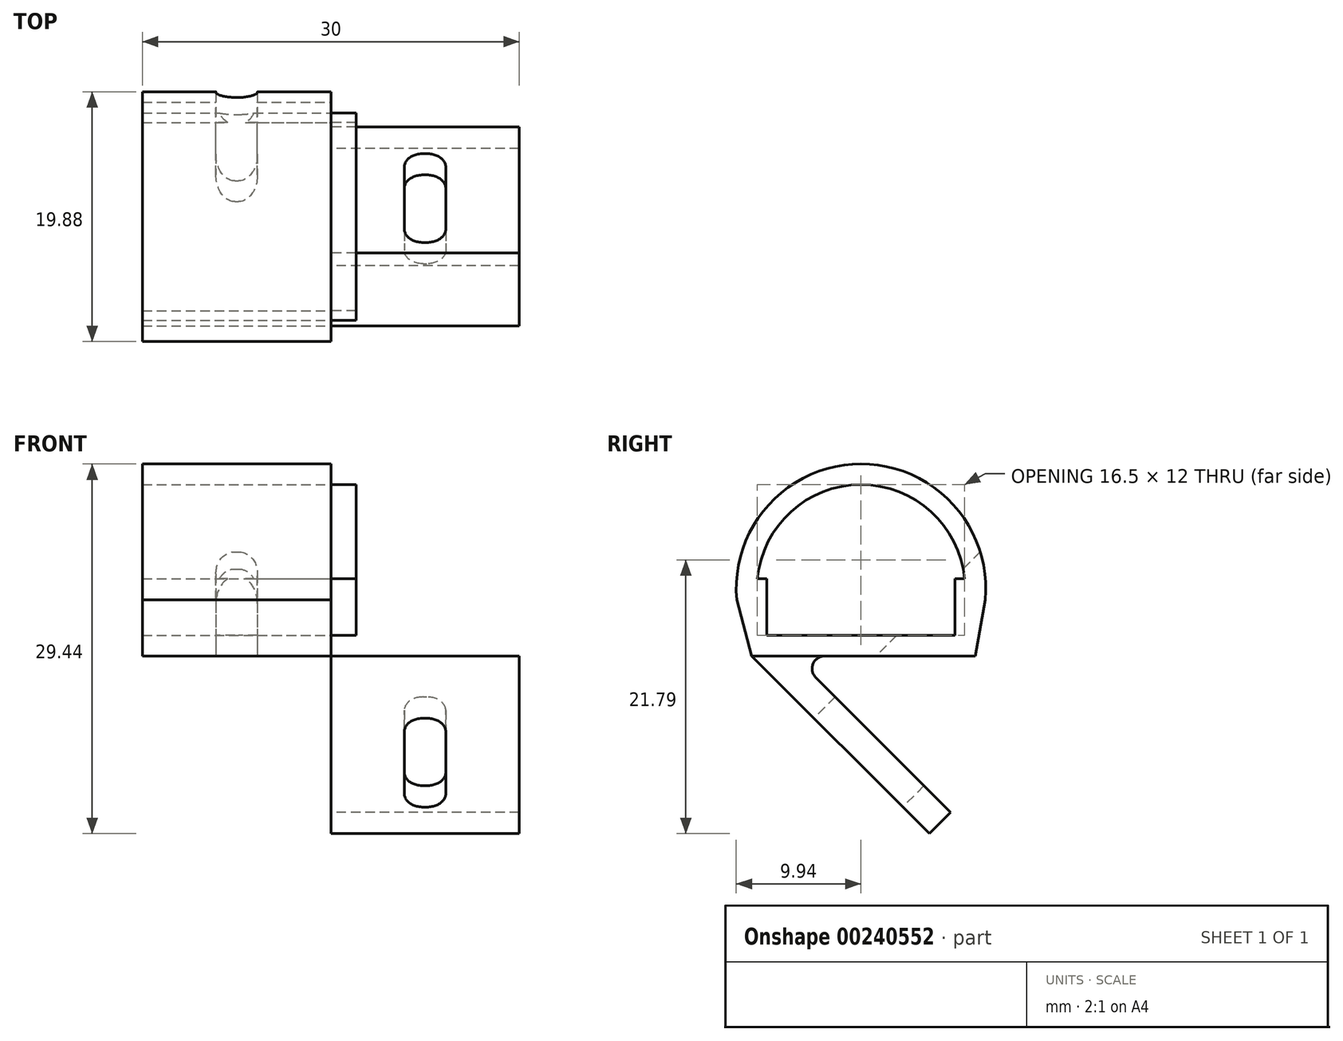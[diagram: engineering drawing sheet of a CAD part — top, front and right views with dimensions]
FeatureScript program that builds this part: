
annotation { "Feature Type Name" : "Feature", "Feature Type Description" : "" }
export const myFeature = defineFeature(function(context is Context, id is Id, definition is map)
    precondition{}
    {
        {
            var Q0;
            Q0=qCreatedBy(makeId("Right.planeOp"),FACE);
            var sketch = newSketch(context, id + "F0", { "sketchPlane" : qUnion([Q0])});
            skLineSegment(sketch, "E0.top", {"start": v(-7.5, -4.5) * mm, "end": v(7.5, -4.5) * mm});
            skLineSegment(sketch, "E0.left", {"start": v(-7.5, 0) * mm, "end": v(-7.5, -4.5) * mm});
            skLineSegment(sketch, "E0.right", {"start": v(7.5, 0) * mm, "end": v(7.5, -4.5) * mm});
            skLineSegment(sketch, "E1", {"start": v(-8.25, 0) * mm, "end": v(-7.5, 0) * mm});
            skArc(sketch, "E2", {"start": v(8.25, 0) * mm, "mid": v(0, 7.5) * mm, "end": v(-8.25, 0) * mm});
            skLineSegment(sketch, "E3", {"start": v(7.5, 0) * mm, "end": v(8.25, 0) * mm});
            skArc(sketch, "E4.3", {"start": v(9.9, -1.68) * mm, "mid": v(0, 9.15) * mm, "end": v(-9.9, -1.68) * mm});
            skLineSegment(sketch, "E4.4", {"start": v(-8.7, -6.15) * mm, "end": v(9.1, -6.15) * mm});
            skLineSegment(sketch, "E5", {"start": v(-9.9, -1.68) * mm, "end": v(-8.7, -6.15) * mm});
            skLineSegment(sketch, "E6", {"start": v(9.9, -1.68) * mm, "end": v(9.1, -6.15) * mm});
            skSolve(sketch);
        }
        {
            var Q0;
            Q0=makeQuery(id+"F0.imprint","IMPRINT",FACE,{"disambiguationData":[TD([[makeQuery(id+"F0.imprint","IMPRINT",EDGE,{"derivedFrom":sQuery(id+"F0.wireOp",EDGE,"E0.top")}),-1.0]])]});
            extrude(context, id + "F1", {"entities" : qUnion([Q0]), "depth" : 15 * mm});
        }
        {
            var Q0;
            Q0=makeQuery(id+"F0.imprint","IMPRINT",FACE,{"disambiguationData":[TD([[makeQuery(id+"F0.imprint","IMPRINT",EDGE,{"derivedFrom":sQuery(id+"F0.wireOp",EDGE,"E0.top")}),1.0]])]});
            extrude(context, id + "F2", {"entities" : qUnion([Q0]), "depth" : 2 * mm});
        }
        {
            var Q0;
            Q0=qCreatedBy(makeId("Right.planeOp"),FACE);
            var sketch = newSketch(context, id + "F3", { "sketchPlane" : qUnion([Q0])});
            skLineSegment(sketch, "E7.0", {"start": v(-2.9, -6.15) * mm, "end": v(9.1, -6.15) * mm});
            skLineSegment(sketch, "E8", {"start": v(-8.7, -6.15) * mm, "end": v(5.44, -20.3) * mm});
            skLineSegment(sketch, "E9", {"start": v(5.44, -20.3) * mm, "end": v(7.14, -18.6) * mm});
            skLineSegment(sketch, "E10", {"start": v(7.14, -18.6) * mm, "end": v(-3.6, -7.86) * mm});
            skPoint(sketch, "E11.newPointB", {"position": v(-8.7, -6.15) * mm});
            skArc(sketch, "E11.filletArc", {"start": v(-2.9, -6.15) * mm, "mid": v(-3.82, -6.77) * mm, "end": v(-3.6, -7.86) * mm});
            skLineSegment(sketch, "E12", {"start": v(-8.7, -6.15) * mm, "end": v(-2.9, -6.15) * mm});
            skSolve(sketch);
        }
        {
            var Q0;
            Q0=makeQuery(id+"F3.imprint","IMPRINT",FACE,{"disambiguationData":[TD([[makeQuery(id+"F3.imprint","IMPRINT",EDGE,{"derivedFrom":sQuery(id+"F3.wireOp",EDGE,"E8")}),1.0]])]});
            extrude(context, id + "F4", {"entities" : qUnion([Q0]), "depth" : 15 * mm});
        }
        {
            var Q0;
            Q0=makeQuery(id+"F4.opExtrude","SWEPT_FACE",FACE,{"disambiguationData":[OSD([sQuery(id+"F3.wireOp",EDGE,"E8")])]});
            var sketch = newSketch(context, id + "F5", { "sketchPlane" : qUnion([Q0])});
            skLineSegment(sketch, "E13.bottom", {"start": v(7.35, -15.2) * mm, "end": v(7.65, -15.2) * mm});
            skLineSegment(sketch, "E13.top", {"start": v(7.35, -5.2) * mm, "end": v(7.65, -5.2) * mm});
            skLineSegment(sketch, "E13.left", {"start": v(5.85, -13.7) * mm, "end": v(5.85, -6.7) * mm});
            skLineSegment(sketch, "E13.right", {"start": v(9.15, -13.7) * mm, "end": v(9.15, -6.7) * mm});
            skLineSegment(sketch, "E14.0.0", {"start": v(0, 1.8) * mm, "end": v(0, -18.2) * mm});
            skLineSegment(sketch, "E14.0.1", {"start": v(0, -18.2) * mm, "end": v(15, -18.2) * mm});
            skLineSegment(sketch, "E14.0.2", {"start": v(15, -18.2) * mm, "end": v(15, 1.8) * mm});
            skLineSegment(sketch, "E14.0.3", {"start": v(15, 1.8) * mm, "end": v(0, 1.8) * mm});
            skPoint(sketch, "E15.visualSharp", {"position": v(5.85, -15.2) * mm});
            skArc(sketch, "E15.filletArc", {"start": v(5.85, -13.7) * mm, "mid": v(6.29, -14.76) * mm, "end": v(7.35, -15.2) * mm});
            skPoint(sketch, "E16.visualSharp", {"position": v(9.15, -15.2) * mm});
            skArc(sketch, "E16.filletArc", {"start": v(7.65, -15.2) * mm, "mid": v(8.71, -14.76) * mm, "end": v(9.15, -13.7) * mm});
            skPoint(sketch, "E17.visualSharp", {"position": v(9.15, -5.2) * mm});
            skArc(sketch, "E17.filletArc", {"start": v(9.15, -6.7) * mm, "mid": v(8.71, -5.64) * mm, "end": v(7.65, -5.2) * mm});
            skPoint(sketch, "E18.visualSharp", {"position": v(5.85, -5.2) * mm});
            skArc(sketch, "E18.filletArc", {"start": v(7.35, -5.2) * mm, "mid": v(6.29, -5.64) * mm, "end": v(5.85, -6.7) * mm});
            skSolve(sketch);
        }
        {
            var Q0;
            Q0=makeQuery(id+"F5.imprint","IMPRINT",FACE,{"disambiguationData":[TD([[makeQuery(id+"F5.imprint","IMPRINT",EDGE,{"derivedFrom":sQuery(id+"F5.wireOp",EDGE,"E13.bottom")}),1.0]])]});
            extrude(context, id + "F6", {"entities" : qUnion([Q0]), "operationType" : NewBodyOperationType.REMOVE, "oppositeDirection" : true, "depth" : 25 * mm});
        }
        {
            var Q0;
            Q0=makeQuery(id+"F1.opExtrude","SWEPT_BODY",BODY,{"disambiguationData":[OSD([sQuery(id+"F0.wireOp",EDGE,"E0.top"),sQuery(id+"F0.wireOp",EDGE,"E0.left"),sQuery(id+"F0.wireOp",EDGE,"E0.right"),sQuery(id+"F0.wireOp",EDGE,"E1"),sQuery(id+"F0.wireOp",EDGE,"E2"),sQuery(id+"F0.wireOp",EDGE,"E3"),sQuery(id+"F0.wireOp",EDGE,"E4.3"),sQuery(id+"F0.wireOp",EDGE,"E4.4"),sQuery(id+"F0.wireOp",EDGE,"E5"),sQuery(id+"F0.wireOp",EDGE,"E6")])]});
            var Q1;
            Q1=qCreatedBy(makeId("Right.planeOp"),FACE);
            mirror(context, id + "F7", {"entities" : qUnion([Q0]), "mirrorPlane" : qUnion([Q1])});
        }
        {
            var Q0;
            Q0=makeQuery(id+"F1.opExtrude","SWEPT_BODY",BODY,{"disambiguationData":[OSD([sQuery(id+"F0.wireOp",EDGE,"E0.top"),sQuery(id+"F0.wireOp",EDGE,"E0.left"),sQuery(id+"F0.wireOp",EDGE,"E0.right"),sQuery(id+"F0.wireOp",EDGE,"E1"),sQuery(id+"F0.wireOp",EDGE,"E2"),sQuery(id+"F0.wireOp",EDGE,"E3"),sQuery(id+"F0.wireOp",EDGE,"E4.3"),sQuery(id+"F0.wireOp",EDGE,"E4.4"),sQuery(id+"F0.wireOp",EDGE,"E5"),sQuery(id+"F0.wireOp",EDGE,"E6")])]});
            deleteBodies(context, id + "F8", {"entities" : qUnion([Q0])});
        }
    });
